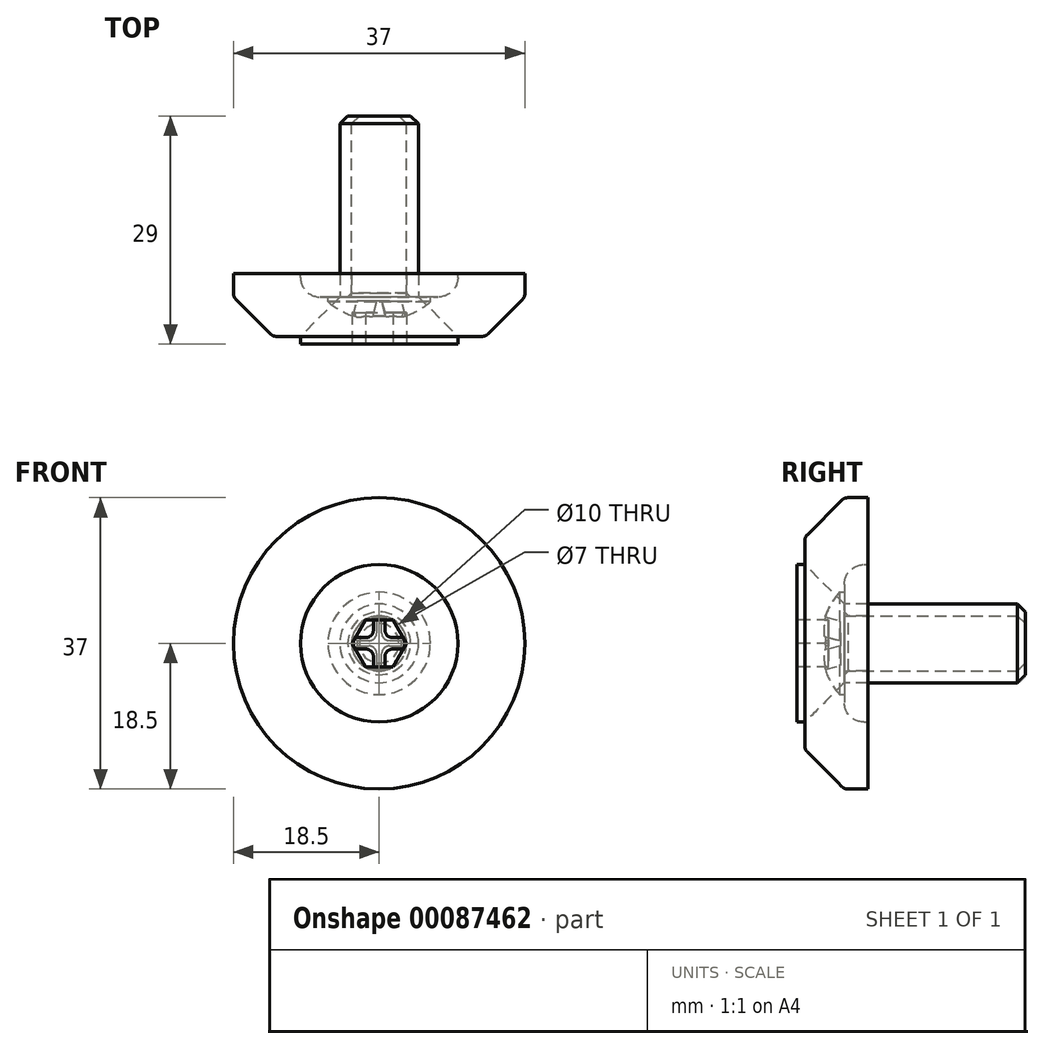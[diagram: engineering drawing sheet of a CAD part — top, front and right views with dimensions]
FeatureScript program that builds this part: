
annotation { "Feature Type Name" : "Feature", "Feature Type Description" : "" }
export const myFeature = defineFeature(function(context is Context, id is Id, definition is map)
    precondition{}
    {
        {
            var Q0;
            Q0=qCreatedBy(makeId("Top.planeOp"),FACE);
            var sketch = newSketch(context, id + "F0", { "sketchPlane" : qUnion([Q0])});
            skLineSegment(sketch, "E0", {"start": v(0, 0) * mm, "end": v(0, 50) * mm, "construction": true});
            skSolve(sketch);
        }
        {
            var Q0;
            Q0=qCreatedBy(makeId("Front.planeOp"),FACE);
            var sketch = newSketch(context, id + "F1", { "sketchPlane" : qUnion([Q0])});
            skLineSegment(sketch, "E1", {"start": v(0, 0) * mm, "end": v(0, 50) * mm, "construction": true});
            skSolve(sketch);
        }
        {
            var Q0;
            Q0=qCreatedBy(makeId("Right.planeOp"),FACE);
            var sketch = newSketch(context, id + "F2", { "sketchPlane" : qUnion([Q0])});
            skLineSegment(sketch, "E2.0", {"start": v(0, 0) * mm, "end": v(50, 0) * mm, "construction": true});
            skLineSegment(sketch, "E3", {"start": v(0, 0) * mm, "end": v(0, 10) * mm});
            skLineSegment(sketch, "E4", {"start": v(0, 10) * mm, "end": v(-0.5, 10) * mm});
            skLineSegment(sketch, "E5", {"start": v(0, 0) * mm, "end": v(-3, 0) * mm});
            skArc(sketch, "E6", {"start": v(-0.5, 10) * mm, "mid": v(-2.27, 9.27) * mm, "end": v(-3, 7.5) * mm});
            skLineSegment(sketch, "E7", {"start": v(-3, 7.5) * mm, "end": v(-3, 0) * mm});
            skSolve(sketch);
        }
        {
            var Q0;
            Q0=makeQuery(id+"F2.imprint","IMPRINT",FACE,{"disambiguationData":[TD([[makeQuery(id+"F2.imprint","IMPRINT",EDGE,{"derivedFrom":sQuery(id+"F2.wireOp",EDGE,"E3")}),1.0]])]});
            var Q1;
            Q1=sQuery(id+"F2.wireOp",EDGE,"E5");
            revolve(context, id + "F3", {"entities" : qUnion([Q0]), "axis" : qUnion([Q1]), "revolveType" : RevolveType.FULL});
        }
        {
            var Q0;
            Q0=makeQuery(id+"F3.opRevolve","SWEPT_FACE",FACE,{"disambiguationData":[OSD([sQuery(id+"F2.wireOp",EDGE,"E7")])]});
            var sketch = newSketch(context, id + "F4", { "sketchPlane" : qUnion([Q0])});
            skPoint(sketch, "E8", {"position": v(0, 0) * mm});
            skSolve(sketch);
        }
        {
            var Q0;
            Q0=sQuery(id+"F4.wireOp",VERTEX,"E8");
            var Q1;
            Q1=makeQuery(id+"F3.opRevolve","SWEPT_BODY",BODY,{"disambiguationData":[OSD([sQuery(id+"F2.wireOp",EDGE,"E3"),sQuery(id+"F2.wireOp",EDGE,"E4"),sQuery(id+"F2.wireOp",EDGE,"E5"),sQuery(id+"F2.wireOp",EDGE,"E6"),sQuery(id+"F2.wireOp",EDGE,"E7")])]});
            hole(context, id + "F5", {"style" : HoleStyle.C_SINK, "endStyle" : HoleEndStyle.THROUGH, "holeDiameter" : 7 * mm, "cSinkDiameter" : 8 * mm, "cSinkAngle" : 90 * degree, "startFromSketch" : true, "locations" : qUnion([Q0]), "scope" : qUnion([Q1]), "isTappedThrough" : true});
        }
        {
            var Q0;
            Q0=qCreatedBy(makeId("Right.planeOp"),FACE);
            var sketch = newSketch(context, id + "F6", { "sketchPlane" : qUnion([Q0])});
            skLineSegment(sketch, "E9", {"start": v(0, 0) * mm, "end": v(0, 18.5) * mm});
            skLineSegment(sketch, "E10", {"start": v(0, 18.5) * mm, "end": v(-3, 18.5) * mm});
            skLineSegment(sketch, "E11", {"start": v(-3, 18.5) * mm, "end": v(-8, 13.5) * mm});
            skLineSegment(sketch, "E12", {"start": v(-8, 13.5) * mm, "end": v(-8, 0) * mm});
            skLineSegment(sketch, "E13", {"start": v(-8, 0) * mm, "end": v(0, 0) * mm});
            skLineSegment(sketch, "E14.0", {"start": v(0, 0) * mm, "end": v(50, 0) * mm, "construction": true});
            skSolve(sketch);
        }
        {
            var Q0;
            Q0=makeQuery(id+"F6.imprint","IMPRINT",FACE,{"disambiguationData":[TD([[makeQuery(id+"F6.imprint","IMPRINT",EDGE,{"derivedFrom":sQuery(id+"F6.wireOp",EDGE,"E9")}),1.0]])]});
            var Q1;
            Q1=sQuery(id+"F6.wireOp",EDGE,"E13");
            revolve(context, id + "F7", {"entities" : qUnion([Q0]), "axis" : qUnion([Q1]), "revolveType" : RevolveType.FULL});
        }
        {
            var Q0;
            Q0=makeQuery(id+"F7.opRevolve","SWEPT_FACE",FACE,{"disambiguationData":[OSD([sQuery(id+"F6.wireOp",EDGE,"E12")])]});
            var sketch = newSketch(context, id + "F8", { "sketchPlane" : qUnion([Q0])});
            skPoint(sketch, "E15", {"position": v(0, 0) * mm});
            skSolve(sketch);
        }
        {
            var Q0;
            Q0=sQuery(id+"F8.wireOp",VERTEX,"E15");
            var Q1;
            Q1=makeQuery(id+"F7.opRevolve","SWEPT_BODY",BODY,{"disambiguationData":[OSD([sQuery(id+"F6.wireOp",EDGE,"E9"),sQuery(id+"F6.wireOp",EDGE,"E10"),sQuery(id+"F6.wireOp",EDGE,"E11"),sQuery(id+"F6.wireOp",EDGE,"E12"),sQuery(id+"F6.wireOp",EDGE,"E13")])]});
            hole(context, id + "F9", {"style" : HoleStyle.C_SINK, "endStyle" : HoleEndStyle.THROUGH, "holeDiameter" : 10 * mm, "cSinkDiameter" : 20 * mm, "cSinkAngle" : 90 * degree, "startFromSketch" : true, "locations" : qUnion([Q0]), "scope" : qUnion([Q1]), "isTappedThrough" : true});
        }
        {
            var Q0;
            Q0=makeQuery(id+"F7.opRevolve","SWEPT_FACE",FACE,{"disambiguationData":[OSD([sQuery(id+"F6.wireOp",EDGE,"E11")])]});
            fillet(context, id + "F10", {"entities" : qUnion([Q0]), "radius" : 1 * mm, "tangentPropagation" : true, "allowEdgeOverflow" : false});
        }
        {
            var Q0;
            Q0=qCreatedBy(makeId("Front.planeOp"),FACE);
            cPlane(context, id + "F11", {"entities" : qUnion([Q0]), "cplaneType" : CPlaneType.OFFSET, "offset" : 20 * mm, "oppositeDirection" : true, "width" : 150 * mm, "height" : 150 * mm});
        }
        {
            var Q0;
            Q0=qCreatedBy(makeId("Right.planeOp"),FACE);
            var sketch = newSketch(context, id + "F12", { "sketchPlane" : qUnion([Q0])});
            skLineSegment(sketch, "E16", {"start": v(20, 3.5) * mm, "end": v(-3, 3.5) * mm});
            skLineSegment(sketch, "E17", {"start": v(-3, 3.5) * mm, "end": v(-3, 6.5) * mm});
            skLineSegment(sketch, "E18", {"start": v(-3, 6.5) * mm, "end": v(-3.6, 6.5) * mm});
            skLineSegment(sketch, "E19", {"start": v(20, 3.5) * mm, "end": v(20, 0) * mm});
            skLineSegment(sketch, "E20", {"start": v(20, 0) * mm, "end": v(-6, 0) * mm});
            skArc(sketch, "E21", {"start": v(-3.6, 6.5) * mm, "mid": v(-5.38, 3.46) * mm, "end": v(-6, 0) * mm});
            skLineSegment(sketch, "E22", {"start": v(-2.5, 3.5) * mm, "end": v(0, 3.5) * mm, "construction": true});
            skLineSegment(sketch, "E23.0", {"start": v(0, 0) * mm, "end": v(50, 0) * mm, "construction": true});
            skSolve(sketch);
        }
        {
            var Q0;
            Q0=qSketchRegion(id+"F12",true);
            var Q1;
            Q1=sQuery(id+"F12.wireOp",EDGE,"E20");
            revolve(context, id + "F13", {"entities" : qUnion([Q0]), "axis" : qUnion([Q1]), "revolveType" : RevolveType.FULL});
        }
        {
            var Q0;
            Q0=qCreatedBy(makeId("Front.planeOp"),FACE);
            var Q1;
            Q1=sQuery(id+"F12.wireOp",VERTEX,"E21.end");
            cPlane(context, id + "F14", {"entities" : qUnion([Q0, Q1]), "cplaneType" : CPlaneType.PLANE_POINT, "offset" : 150 * mm, "width" : 150 * mm, "height" : 150 * mm});
        }
        {
            var Q0;
            Q0=qCreatedBy(id+"F14.planeOp",FACE);
            var sketch = newSketch(context, id + "F15", { "sketchPlane" : qUnion([Q0])});
            skLineSegment(sketch, "E24.bottom", {"start": v(1, 3.5) * mm, "end": v(-1, 3.5) * mm});
            skLineSegment(sketch, "E24.top", {"start": v(1, -3.5) * mm, "end": v(-1, -3.5) * mm});
            skLineSegment(sketch, "E24.left", {"start": v(1, 3.5) * mm, "end": v(1, -3.5) * mm});
            skLineSegment(sketch, "E24.right", {"start": v(-1, 3.5) * mm, "end": v(-1, -3.5) * mm});
            skPoint(sketch, "E24.middle", {"position": v(0, 0) * mm});
            skLineSegment(sketch, "E25.bottom", {"start": v(3.5, -1) * mm, "end": v(-3.5, -1) * mm});
            skLineSegment(sketch, "E25.top", {"start": v(3.5, 1) * mm, "end": v(-3.5, 1) * mm});
            skLineSegment(sketch, "E25.left", {"start": v(3.5, -1) * mm, "end": v(3.5, 1) * mm});
            skLineSegment(sketch, "E25.right", {"start": v(-3.5, -1) * mm, "end": v(-3.5, 1) * mm});
            skSolve(sketch);
        }
        {
            var Q0;
            Q0=qSketchRegion(id+"F15",true);
            extrude(context, id + "F16", {"entities" : qUnion([Q0]), "operationType" : NewBodyOperationType.REMOVE, "oppositeDirection" : true, "depth" : 2.5 * mm, "hasDraft" : true, "draftAngle" : 15 * degree, "draftPullDirection" : true});
        }
        {
            var Q0;
            Q0=makeQuery(id+"F16.boolean.opBoolean","COPY",EDGE,{"derivedFrom":makeQuery(id+"F16.opExtrude","SWEPT_EDGE",EDGE,{"disambiguationData":[OSD([sQuery(id+"F15.wireOp",EDGE,"E24.right"),sQuery(id+"F15.wireOp",EDGE,"E25.top")])]})});
            var Q1;
            Q1=makeQuery(id+"F16.boolean.opBoolean","COPY",EDGE,{"derivedFrom":makeQuery(id+"F16.opExtrude","SWEPT_EDGE",EDGE,{"disambiguationData":[OSD([sQuery(id+"F15.wireOp",EDGE,"E24.left"),sQuery(id+"F15.wireOp",EDGE,"E25.top")])]})});
            var Q2;
            Q2=makeQuery(id+"F16.boolean.opBoolean","COPY",EDGE,{"derivedFrom":makeQuery(id+"F16.opExtrude","SWEPT_EDGE",EDGE,{"disambiguationData":[OSD([sQuery(id+"F15.wireOp",EDGE,"E24.left"),sQuery(id+"F15.wireOp",EDGE,"E25.bottom")])]})});
            var Q3;
            Q3=makeQuery(id+"F16.boolean.opBoolean","COPY",EDGE,{"derivedFrom":makeQuery(id+"F16.opExtrude","SWEPT_EDGE",EDGE,{"disambiguationData":[OSD([sQuery(id+"F15.wireOp",EDGE,"E24.right"),sQuery(id+"F15.wireOp",EDGE,"E25.bottom")])]})});
            fillet(context, id + "F17", {"entities" : qUnion([Q0, Q1, Q2, Q3]), "radius" : 1 * mm, "tangentPropagation" : true, "allowEdgeOverflow" : false});
        }
        {
            var Q0;
            Q0=qCreatedBy(makeId("Right.planeOp"),FACE);
            var sketch = newSketch(context, id + "F18", { "sketchPlane" : qUnion([Q0])});
            skLineSegment(sketch, "E26", {"start": v(20, 5) * mm, "end": v(-3, 5) * mm});
            skLineSegment(sketch, "E27", {"start": v(-3, 5) * mm, "end": v(-8, 10) * mm});
            skLineSegment(sketch, "E28", {"start": v(-8, 10) * mm, "end": v(-9, 10) * mm});
            skLineSegment(sketch, "E29", {"start": v(-9, 10) * mm, "end": v(-9, 0) * mm});
            skLineSegment(sketch, "E30", {"start": v(-9, 0) * mm, "end": v(20, 0) * mm});
            skLineSegment(sketch, "E31", {"start": v(20, 0) * mm, "end": v(20, 5) * mm});
            skLineSegment(sketch, "E32", {"start": v(-3, 5) * mm, "end": v(0, 5) * mm, "construction": true});
            skLineSegment(sketch, "E33.0", {"start": v(0, 0) * mm, "end": v(50, 0) * mm, "construction": true});
            skSolve(sketch);
        }
        {
            var Q0;
            Q0=makeQuery(id+"F18.imprint","IMPRINT",FACE,{"disambiguationData":[TD([[makeQuery(id+"F18.imprint","IMPRINT",EDGE,{"derivedFrom":sQuery(id+"F18.wireOp",EDGE,"E26")}),1.0]])]});
            var Q1;
            Q1=sQuery(id+"F18.wireOp",EDGE,"E30");
            revolve(context, id + "F19", {"entities" : qUnion([Q0]), "axis" : qUnion([Q1]), "revolveType" : RevolveType.FULL});
        }
        {
            var Q0;
            Q0=makeQuery(id+"F19.opRevolve","SWEPT_FACE",FACE,{"disambiguationData":[OSD([sQuery(id+"F18.wireOp",EDGE,"E29")])]});
            var sketch = newSketch(context, id + "F20", { "sketchPlane" : qUnion([Q0])});
            skCircle(sketch, "E34.cCircle", {"center": v(0, 0) * mm, "radius": 3 * mm, "construction": true});
            skLineSegment(sketch, "E34.0", {"start": v(-1.73, 3) * mm, "end": v(1.73, 3) * mm});
            skLineSegment(sketch, "E34.1", {"start": v(1.73, 3) * mm, "end": v(3.46, 0) * mm});
            skLineSegment(sketch, "E34.2", {"start": v(3.46, 0) * mm, "end": v(1.73, -3) * mm});
            skLineSegment(sketch, "E34.3", {"start": v(1.73, -3) * mm, "end": v(-1.73, -3) * mm});
            skLineSegment(sketch, "E34.4", {"start": v(-1.73, -3) * mm, "end": v(-3.46, 0) * mm});
            skLineSegment(sketch, "E34.5", {"start": v(-3.46, 0) * mm, "end": v(-1.73, 3) * mm});
            skPoint(sketch, "E34.0.midPoint", {"position": v(0, 3) * mm});
            skSolve(sketch);
        }
        {
            var Q0;
            Q0=qSketchRegion(id+"F20",true);
            extrude(context, id + "F21", {"entities" : qUnion([Q0]), "operationType" : NewBodyOperationType.REMOVE, "oppositeDirection" : true, "depth" : 4 * mm});
        }
        {
            var Q0;
            Q0=makeQuery(id+"F13.opRevolve","SWEPT_EDGE",EDGE,{"disambiguationData":[OSD([sQuery(id+"F12.wireOp",EDGE,"E16"),sQuery(id+"F12.wireOp",EDGE,"E19")])]});
            var Q1;
            Q1=makeQuery(id+"F19.opRevolve","SWEPT_EDGE",EDGE,{"disambiguationData":[OSD([sQuery(id+"F18.wireOp",EDGE,"E26"),sQuery(id+"F18.wireOp",EDGE,"E31")])]});
            chamfer(context, id + "F22", {"entities" : qUnion([Q0, Q1]), "width" : 1 * mm, "tangentPropagation" : true});
        }
    });
